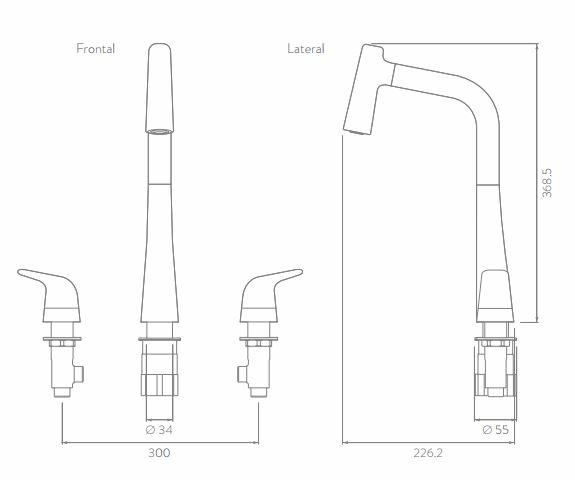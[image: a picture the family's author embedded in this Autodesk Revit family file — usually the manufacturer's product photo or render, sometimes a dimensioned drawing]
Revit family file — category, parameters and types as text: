
# Revit family: LQ5010001_Lavaplatos 8 pulgadas Liquid
name_source: partatom
category: Plumbing Fixtures
units: mm (PartAtom-declared; Revit-internal decimal feet)

## family parameters
Cut with Voids When Loaded = No
Host = Face
OmniClass Number = 23.31.11.00
OmniClass Title = Faucets
Part Type = Normal
Room Calculation Point = No
Round Connector Dimension = Use Diameter
Shared = No

## types (1)
- LQ5010001_Lavaplatos 8 pulgadas Liquid
    Alto = 368 mm  [stored 1.20735 ft]
    Ancho = 416 mm
    CW Connection = Yes
    Capacidad de flujo estimada real a 60 psi = 5,6 L/min.
    Creado por = IDD
    Default Elevation = 1219 mm
    Description = La línea de griferías, duchas y accesorios Liquid se inspira en la tensión superficial del agua
y en cómo esta crea formas armoniosas adaptándose al ambiente. Al igual que el agua,
las superficies de las griferías Liquid juegan con la luz y los reflejos que fluyen alrededor
de sus formas, sus líneas continuas y simplicidad formal proporcionan la ventaja práctica,
limpieza sin esfuerzo
    Diámetro desagüe = 15 mm  [stored 0.0492126 ft]
    Fabrication place = Colombia
    Fecha de creación = 13/08/2020
    HW Connection = Yes
    Manufacturer = Corona
    Material = Corona_Metálico
    Peso  Bruto = 2.600 g. - 5,73 lb.
    Peso neto = .350 g. - 5,18 lb.
    Presion maxima = 125 psi (860 Kpa).
    Presion minima = 20 psi (140 Kpa).
    Profundidad = 226 mm  [stored 0.74147 ft]
    Reference = LQ5010001
    Temperatura máxima de trabajo = 71°C / 159,8°F
    Temperatura mínima de Trabajo = 5°C / 41 °F
    URL = https://corona.co
    Vida útil o desgaste (unidad) = 500.000 ciclos.
    Warranty = 30 años
    Waste Connection = Yes
    Weight = 2500 g

note: [stored X ft] marks values corroborated as IEEE doubles in the binary element streams (Revit-internal decimal feet)

## geometry (parser evidence)
native form markers: Sweep x5
no freeform markers — native parametric forms only
